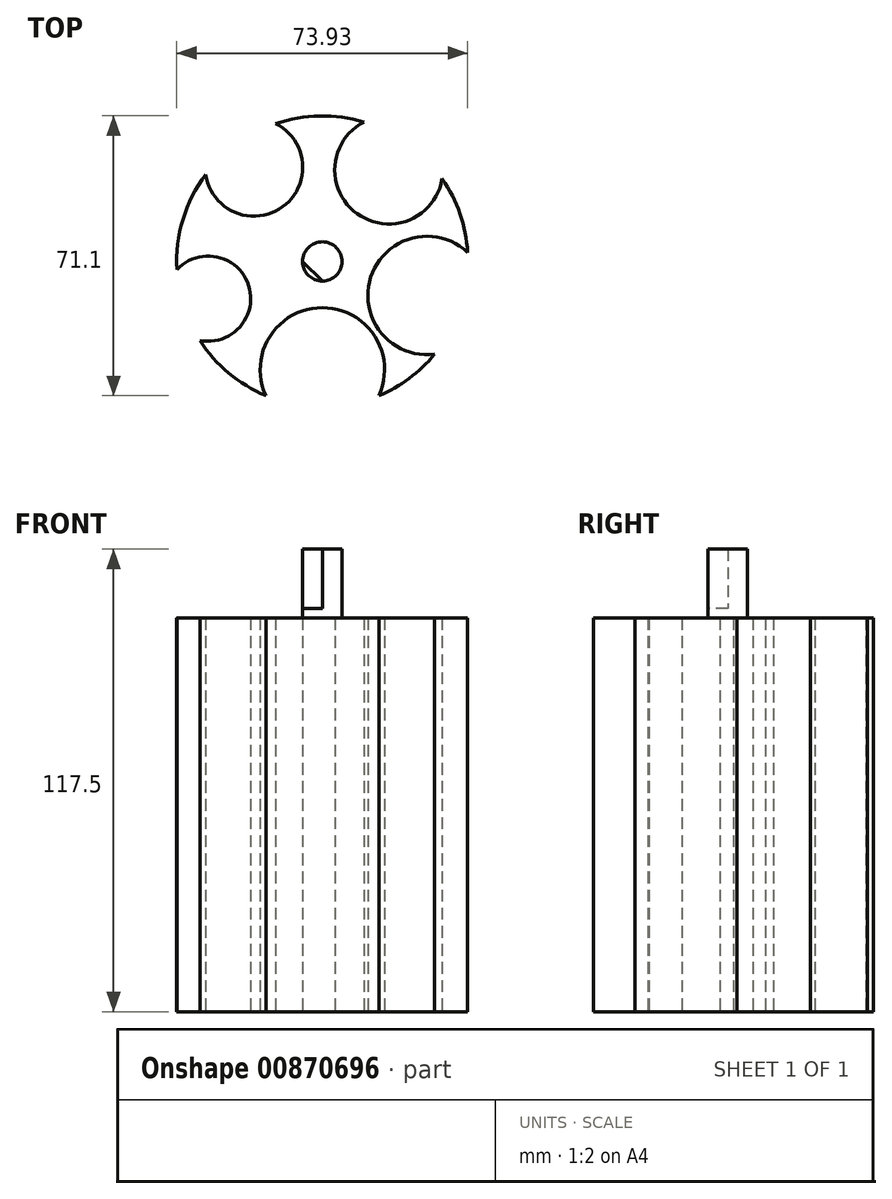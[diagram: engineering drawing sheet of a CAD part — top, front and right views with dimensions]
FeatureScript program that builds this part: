
annotation { "Feature Type Name" : "Feature", "Feature Type Description" : "" }
export const myFeature = defineFeature(function(context is Context, id is Id, definition is map)
    precondition{}
    {
        {
            var Q0;
            Q0=qCreatedBy(makeId("Top.planeOp"),FACE);
            var sketch = newSketch(context, id + "F0", { "sketchPlane" : qUnion([Q0])});
            skCircle(sketch, "E0", {"center": v(0, 0) * mm, "radius": 37 * mm});
            skCircle(sketch, "E1.cCircle", {"center": v(0, 0) * mm, "radius": 22.26 * mm, "construction": true});
            skLineSegment(sketch, "E1.0", {"start": v(26.17, -8.5) * mm, "end": v(0, -27.52) * mm, "construction": true});
            skLineSegment(sketch, "E1.1", {"start": v(0, -27.52) * mm, "end": v(-26.17, -8.5) * mm, "construction": true});
            skLineSegment(sketch, "E1.2", {"start": v(-26.17, -8.5) * mm, "end": v(-16.18, 22.26) * mm, "construction": true});
            skLineSegment(sketch, "E1.3", {"start": v(-16.18, 22.26) * mm, "end": v(16.18, 22.26) * mm, "construction": true});
            skLineSegment(sketch, "E1.4", {"start": v(16.18, 22.26) * mm, "end": v(26.17, -8.5) * mm, "construction": true});
            skPoint(sketch, "E1.0.midPoint", {"position": v(13.09, -18.01) * mm});
            skCircle(sketch, "E2", {"center": v(0, -27.52) * mm, "radius": 15.8 * mm});
            skCircle(sketch, "E3.cCircle", {"center": v(0, 0) * mm, "radius": 22.63 * mm, "construction": true});
            skLineSegment(sketch, "E3.0", {"start": v(26.6, -8.64) * mm, "end": v(0, -27.97) * mm, "construction": true});
            skLineSegment(sketch, "E3.1", {"start": v(0, -27.97) * mm, "end": v(-26.6, -8.64) * mm, "construction": true});
            skLineSegment(sketch, "E3.2", {"start": v(-26.6, -8.64) * mm, "end": v(-16.44, 22.63) * mm, "construction": true});
            skLineSegment(sketch, "E3.3", {"start": v(-16.44, 22.63) * mm, "end": v(16.44, 22.63) * mm, "construction": true});
            skLineSegment(sketch, "E3.4", {"start": v(16.44, 22.63) * mm, "end": v(26.6, -8.64) * mm, "construction": true});
            skPoint(sketch, "E3.0.midPoint", {"position": v(0, -22.63) * mm});
            skCircle(sketch, "E4", {"center": v(26.6, -8.64) * mm, "radius": 15.05 * mm});
            skCircle(sketch, "E5.cCircle", {"center": v(0, 0) * mm, "radius": 23.26 * mm, "construction": true});
            skLineSegment(sketch, "E5.0", {"start": v(0, -28.76) * mm, "end": v(-27.35, -8.89) * mm, "construction": true});
            skLineSegment(sketch, "E5.1", {"start": v(-27.35, -8.89) * mm, "end": v(-16.9, 23.26) * mm, "construction": true});
            skLineSegment(sketch, "E5.2", {"start": v(-16.9, 23.26) * mm, "end": v(16.9, 23.26) * mm, "construction": true});
            skLineSegment(sketch, "E5.3", {"start": v(16.9, 23.26) * mm, "end": v(27.35, -8.89) * mm, "construction": true});
            skLineSegment(sketch, "E5.4", {"start": v(27.35, -8.89) * mm, "end": v(0, -28.76) * mm, "construction": true});
            skPoint(sketch, "E5.0.midPoint", {"position": v(-13.67, -18.82) * mm});
            skCircle(sketch, "E6", {"center": v(16.9, 23.26) * mm, "radius": 13.74 * mm});
            skCircle(sketch, "E7.cCircle", {"center": v(0, 0) * mm, "radius": 23.91 * mm, "construction": true});
            skLineSegment(sketch, "E7.0", {"start": v(-28.11, -9.13) * mm, "end": v(-17.37, 23.91) * mm, "construction": true});
            skLineSegment(sketch, "E7.1", {"start": v(-17.37, 23.91) * mm, "end": v(17.37, 23.91) * mm, "construction": true});
            skLineSegment(sketch, "E7.2", {"start": v(17.37, 23.91) * mm, "end": v(28.11, -9.13) * mm, "construction": true});
            skLineSegment(sketch, "E7.3", {"start": v(28.11, -9.13) * mm, "end": v(0, -29.56) * mm, "construction": true});
            skLineSegment(sketch, "E7.4", {"start": v(0, -29.56) * mm, "end": v(-28.11, -9.13) * mm, "construction": true});
            skPoint(sketch, "E7.0.midPoint", {"position": v(-22.74, 7.4) * mm});
            skCircle(sketch, "E8", {"center": v(-17.37, 23.91) * mm, "radius": 12.4 * mm});
            skCircle(sketch, "E9.cCircle", {"center": v(0, 0) * mm, "radius": 24.68 * mm, "construction": true});
            skLineSegment(sketch, "E9.0", {"start": v(-17.93, 24.68) * mm, "end": v(17.93, 24.68) * mm, "construction": true});
            skLineSegment(sketch, "E9.1", {"start": v(17.93, 24.68) * mm, "end": v(29.02, -9.43) * mm, "construction": true});
            skLineSegment(sketch, "E9.2", {"start": v(29.02, -9.43) * mm, "end": v(0, -30.51) * mm, "construction": true});
            skLineSegment(sketch, "E9.3", {"start": v(0, -30.51) * mm, "end": v(-29.02, -9.43) * mm, "construction": true});
            skLineSegment(sketch, "E9.4", {"start": v(-29.02, -9.43) * mm, "end": v(-17.93, 24.68) * mm, "construction": true});
            skPoint(sketch, "E9.0.midPoint", {"position": v(0, 24.68) * mm});
            skCircle(sketch, "E10", {"center": v(-29.02, -9.43) * mm, "radius": 10.82 * mm});
            skSolve(sketch);
        }
        {
            var Q0;
            {var subQ1=sQuery(id+"F0.wireOp",EDGE,"E0");var subQ9=sQuery(id+"F0.wireOp",EDGE,"E6");var subQ11=makeQuery(id+"F0.imprint","INTERSECT",VERTEX,{"disambiguationData":[OD(0.0)],"derivedFrom":[subQ1,subQ9]});Q0=makeQuery(id+"F0.imprint","IMPRINT",FACE,{"disambiguationData":[TD([[makeQuery(id+"F0.imprint","IMPRINT",EDGE,{"disambiguationData":[TD([[subQ11,1.0]])],"derivedFrom":subQ1}),1.0]])]});}
            extrude(context, id + "F1", {"entities" : qUnion([Q0]), "depth" : 100 * mm, "offsetDistance" : 25 * mm});
        }
        {
            var Q0;
            Q0=makeQuery(id+"F1.opExtrude","CAP_FACE",FACE,{"disambiguationData":[OSD([sQuery(id+"F0.wireOp",EDGE,"E0"),sQuery(id+"F0.wireOp",EDGE,"E2"),sQuery(id+"F0.wireOp",EDGE,"E4"),sQuery(id+"F0.wireOp",EDGE,"E6"),sQuery(id+"F0.wireOp",EDGE,"E8"),sQuery(id+"F0.wireOp",EDGE,"E10")])],"isStart":false});
            cPlane(context, id + "F2", {"entities" : qUnion([Q0]), "cplaneType" : CPlaneType.OFFSET, "offset" : 0 * mm, "width" : 150 * mm, "height" : 150 * mm});
        }
        {
            var Q0;
            Q0=qCreatedBy(id+"F2.planeOp",FACE);
            var sketch = newSketch(context, id + "F3", { "sketchPlane" : qUnion([Q0])});
            skCircle(sketch, "E11", {"center": v(0, 0) * mm, "radius": 5 * mm});
            skLineSegment(sketch, "E12", {"start": v(-5, 0) * mm, "end": v(0, -5) * mm});
            skSolve(sketch);
        }
        {
            var Q0;
            {var subQ0=sQuery(id+"F3.wireOp",EDGE,"E12");Q0=makeQuery(id+"F3.imprint","IMPRINT",FACE,{"disambiguationData":[TD([[makeQuery(id+"F3.imprint","IMPRINT",EDGE,{"derivedFrom":subQ0}),1.0]])]});}
            extrude(context, id + "F4", {"entities" : qUnion([Q0]), "operationType" : NewBodyOperationType.ADD, "depth" : 17.5 * mm, "offsetDistance" : 25 * mm});
        }
        {
            var Q0;
            {var subQ0=sQuery(id+"F3.wireOp",EDGE,"E12");Q0=makeQuery(id+"F3.imprint","IMPRINT",FACE,{"disambiguationData":[TD([[makeQuery(id+"F3.imprint","IMPRINT",EDGE,{"derivedFrom":subQ0}),-1.0]])]});}
            extrude(context, id + "F5", {"entities" : qUnion([Q0]), "operationType" : NewBodyOperationType.ADD, "depth" : 2.5 * mm, "offsetDistance" : 25 * mm});
        }
    });
